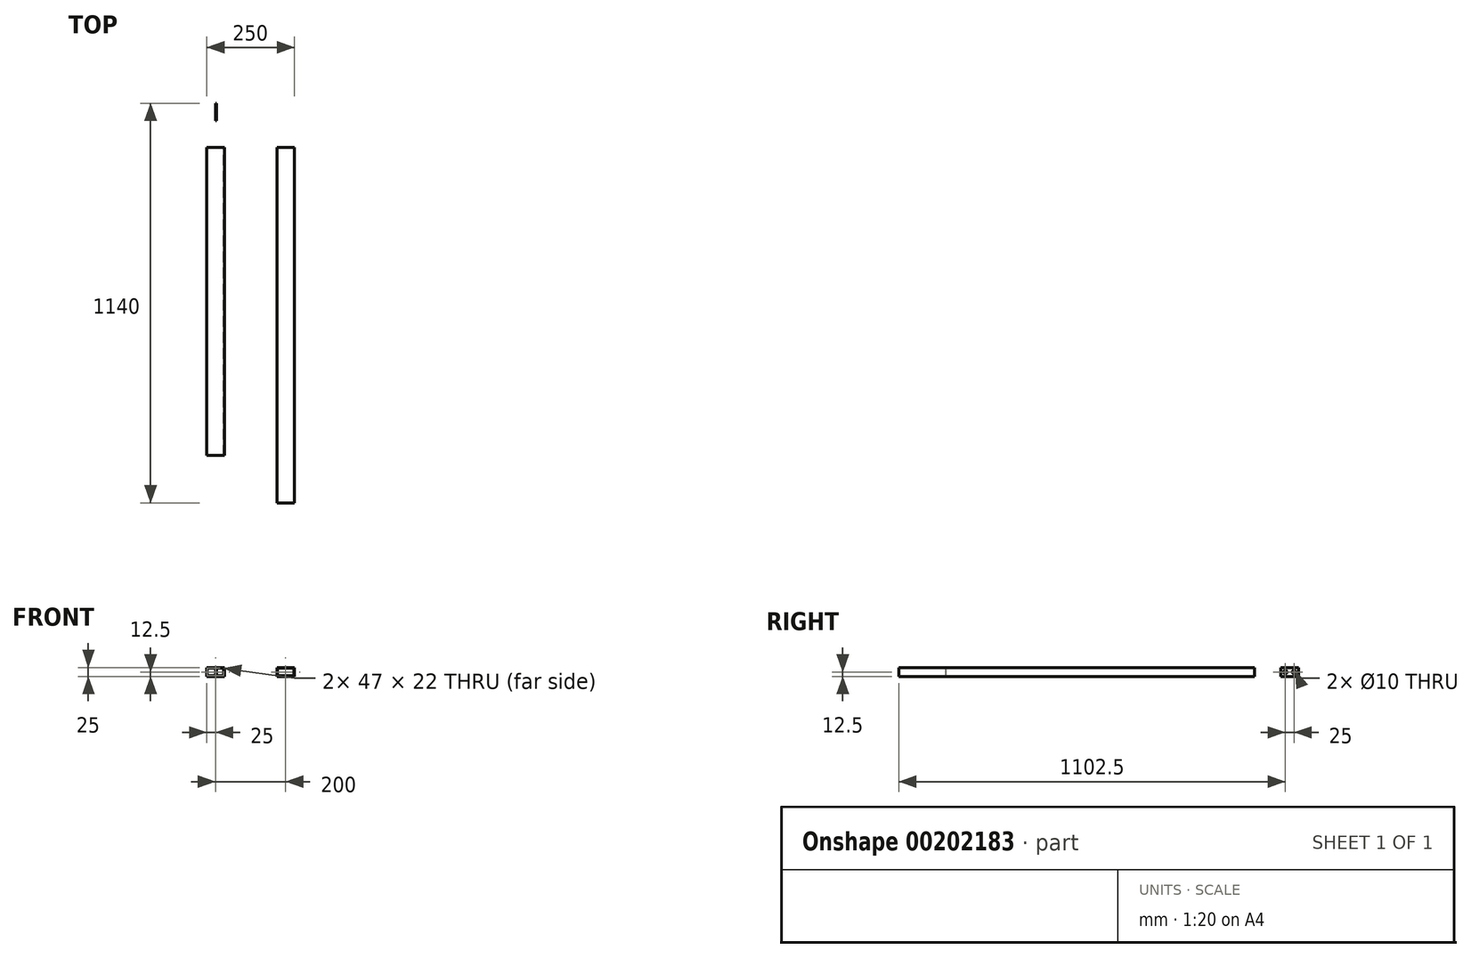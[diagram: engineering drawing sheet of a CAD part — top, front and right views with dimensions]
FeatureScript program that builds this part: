
annotation { "Feature Type Name" : "Feature", "Feature Type Description" : "" }
export const myFeature = defineFeature(function(context is Context, id is Id, definition is map)
    precondition{}
    {
        {
            var Q0;
            Q0=qCreatedBy(makeId("Front.planeOp"),FACE);
            var sketch = newSketch(context, id + "F0", { "sketchPlane" : qUnion([Q0])});
            skLineSegment(sketch, "E0.bottom", {"start": v(25, -12.5) * mm, "end": v(-25, -12.5) * mm});
            skLineSegment(sketch, "E0.top", {"start": v(25, 12.5) * mm, "end": v(-25, 12.5) * mm});
            skLineSegment(sketch, "E0.left", {"start": v(25, -12.5) * mm, "end": v(25, 12.5) * mm});
            skLineSegment(sketch, "E0.right", {"start": v(-25, -12.5) * mm, "end": v(-25, 12.5) * mm});
            skPoint(sketch, "E0.middle", {"position": v(0, 0) * mm});
            skLineSegment(sketch, "E1.bottom", {"start": v(23.5, -11) * mm, "end": v(-23.5, -11) * mm});
            skLineSegment(sketch, "E1.top", {"start": v(23.5, 11) * mm, "end": v(-23.5, 11) * mm});
            skLineSegment(sketch, "E1.left", {"start": v(23.5, -11) * mm, "end": v(23.5, 11) * mm});
            skLineSegment(sketch, "E1.right", {"start": v(-23.5, -11) * mm, "end": v(-23.5, 11) * mm});
            skSolve(sketch);
        }
        {
            var Q0;
            Q0=makeQuery(id+"F0.imprint","IMPRINT",FACE,{"disambiguationData":[TD([[makeQuery(id+"F0.imprint","IMPRINT",EDGE,{"derivedFrom":sQuery(id+"F0.wireOp",EDGE,"E0.bottom")}),-1.0]])]});
            extrude(context, id + "F1", {"entities" : qUnion([Q0]), "depth" : 880 * mm});
        }
        {
            var Q0;
            Q0=qCreatedBy(makeId("Right.planeOp"),FACE);
            var sketch = newSketch(context, id + "F2", { "sketchPlane" : qUnion([Q0])});
            skLineSegment(sketch, "E2", {"start": v(0, 0) * mm, "end": v(100, 0) * mm, "construction": true});
            skLineSegment(sketch, "E3.bottom", {"start": v(125, -12.5) * mm, "end": v(75, -12.5) * mm});
            skLineSegment(sketch, "E3.top", {"start": v(125, 12.5) * mm, "end": v(75, 12.5) * mm});
            skLineSegment(sketch, "E3.left", {"start": v(125, -12.5) * mm, "end": v(125, 12.5) * mm});
            skLineSegment(sketch, "E3.right", {"start": v(75, -12.5) * mm, "end": v(75, 12.5) * mm});
            skPoint(sketch, "E3.middle", {"position": v(100, 0) * mm});
            skLineSegment(sketch, "E4", {"start": v(125, 0) * mm, "end": v(112.5, 0) * mm, "construction": true});
            skPoint(sketch, "E4.endSnap0", {"position": v(75, 0) * mm});
            skPoint(sketch, "E5", {"position": v(112.5, 0) * mm});
            skLineSegment(sketch, "E6", {"start": v(75, 0) * mm, "end": v(87.5, 0) * mm, "construction": true});
            skPoint(sketch, "E7", {"position": v(87.5, 0) * mm});
            skSolve(sketch);
        }
        {
            var Q0;
            Q0=qSketchRegion(id+"F2",true);
            extrude(context, id + "F3", {"entities" : qUnion([Q0]), "depth" : 3 * mm});
        }
        {
            var Q0;
            Q0=sQuery(id+"F2.wireOp",VERTEX,"E7");
            var Q1;
            Q1=sQuery(id+"F2.wireOp",VERTEX,"E5");
            var Q2;
            Q2=makeQuery(id+"F3.opExtrude","SWEPT_BODY",BODY,{"disambiguationData":[OSD([sQuery(id+"F2.wireOp",EDGE,"E3.bottom"),sQuery(id+"F2.wireOp",EDGE,"E3.top"),sQuery(id+"F2.wireOp",EDGE,"E3.left"),sQuery(id+"F2.wireOp",EDGE,"E3.right")])]});
            hole(context, id + "F4", {"style" : HoleStyle.SIMPLE, "endStyle" : HoleEndStyle.THROUGH, "oppositeDirection" : true, "holeDiameter" : 10 * mm, "locations" : qUnion([Q0, Q1]), "scope" : qUnion([Q2]), "isTappedThrough" : true});
        }
        {
            var Q0;
            Q0=qCreatedBy(makeId("Front.planeOp"),FACE);
            var sketch = newSketch(context, id + "F5", { "sketchPlane" : qUnion([Q0])});
            skLineSegment(sketch, "E8.bottom", {"start": v(225, -12.5) * mm, "end": v(175, -12.5) * mm});
            skLineSegment(sketch, "E8.top", {"start": v(225, 12.5) * mm, "end": v(175, 12.5) * mm});
            skLineSegment(sketch, "E8.left", {"start": v(225, -12.5) * mm, "end": v(225, 12.5) * mm});
            skLineSegment(sketch, "E8.right", {"start": v(175, -12.5) * mm, "end": v(175, 12.5) * mm});
            skPoint(sketch, "E8.middle", {"position": v(200, 0) * mm});
            skLineSegment(sketch, "E9.bottom", {"start": v(223.5, -11) * mm, "end": v(176.5, -11) * mm});
            skLineSegment(sketch, "E9.top", {"start": v(223.5, 11) * mm, "end": v(176.5, 11) * mm});
            skLineSegment(sketch, "E9.left", {"start": v(223.5, -11) * mm, "end": v(223.5, 11) * mm});
            skLineSegment(sketch, "E9.right", {"start": v(176.5, -11) * mm, "end": v(176.5, 11) * mm});
            skLineSegment(sketch, "E10", {"start": v(200, 0) * mm, "end": v(0, 0) * mm, "construction": true});
            skSolve(sketch);
        }
        {
            var Q0;
            Q0=qSketchRegion(id+"F5",true);
            extrude(context, id + "F6", {"entities" : qUnion([Q0]), "depth" : 1015 * mm});
        }
    });
